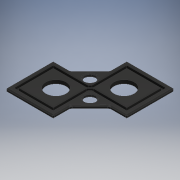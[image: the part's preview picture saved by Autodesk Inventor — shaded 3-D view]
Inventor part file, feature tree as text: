
AUTODESK INVENTOR PART (.ipt)
format: ipt  version: 2018 (Build 220112000, 112)  size: 881,152 bytes
history: native  units: mm
features: other x2, extrude x1, sketch x1
ambient origin geometry x8: Origin, YZ Plane, XZ Plane, XY Plane, X Axis, Y Axis, Z Axis, Center Point
bodies: Solid1 (feature_tree)
feature tree (4):
  other  "29mm_Parasitic_Element"
  other  "MeshFeature1"
  extrude  "Extrusion1"  Depth=2.62mm
  sketch  "Sketch1"  dims[d0=15.0mm d1=22.0mm d2=15.0mm d3=22.0mm d4=2.62mm d5=0.0mm]
